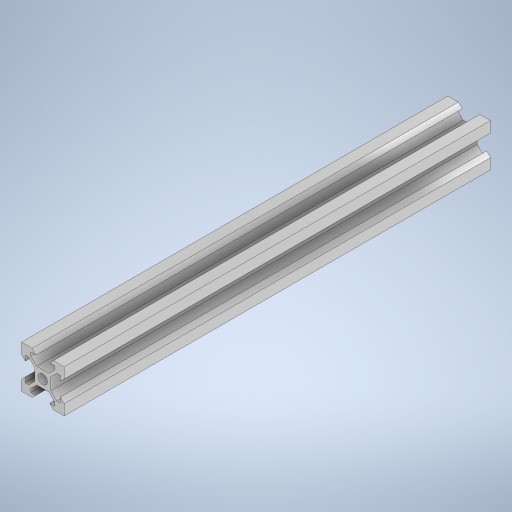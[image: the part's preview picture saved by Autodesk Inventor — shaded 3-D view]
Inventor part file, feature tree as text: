
AUTODESK INVENTOR PART (.ipt)
format: ipt  version: 2024.2 (Build 282272000, 272)  size: 313,856 bytes
history: native  units: mm
features: extrude x1, sketch x1
ambient origin geometry x8: Origin, YZ Plane, XZ Plane, XY Plane, X Axis, Y Axis, Z Axis, Center Point
bodies: Solid1 (feature_tree)
feature tree (2):
  extrude  "Extrusion1"  Depth=200.0mm
  sketch  "Sketch1"  dims[d16=10.0mm d19=3.2mm d21=4.4mm d22=4.4mm d24=45.0deg d25=1.8mm d27=1.8mm d28=45.0deg d29=3.2mm d31=1.4mm d33=2.15mm d34=3.825mm d35=3.825mm d36=135.0deg d37=40.0mm d39=360.0deg d41=200.0mm d42=0.0mm]
